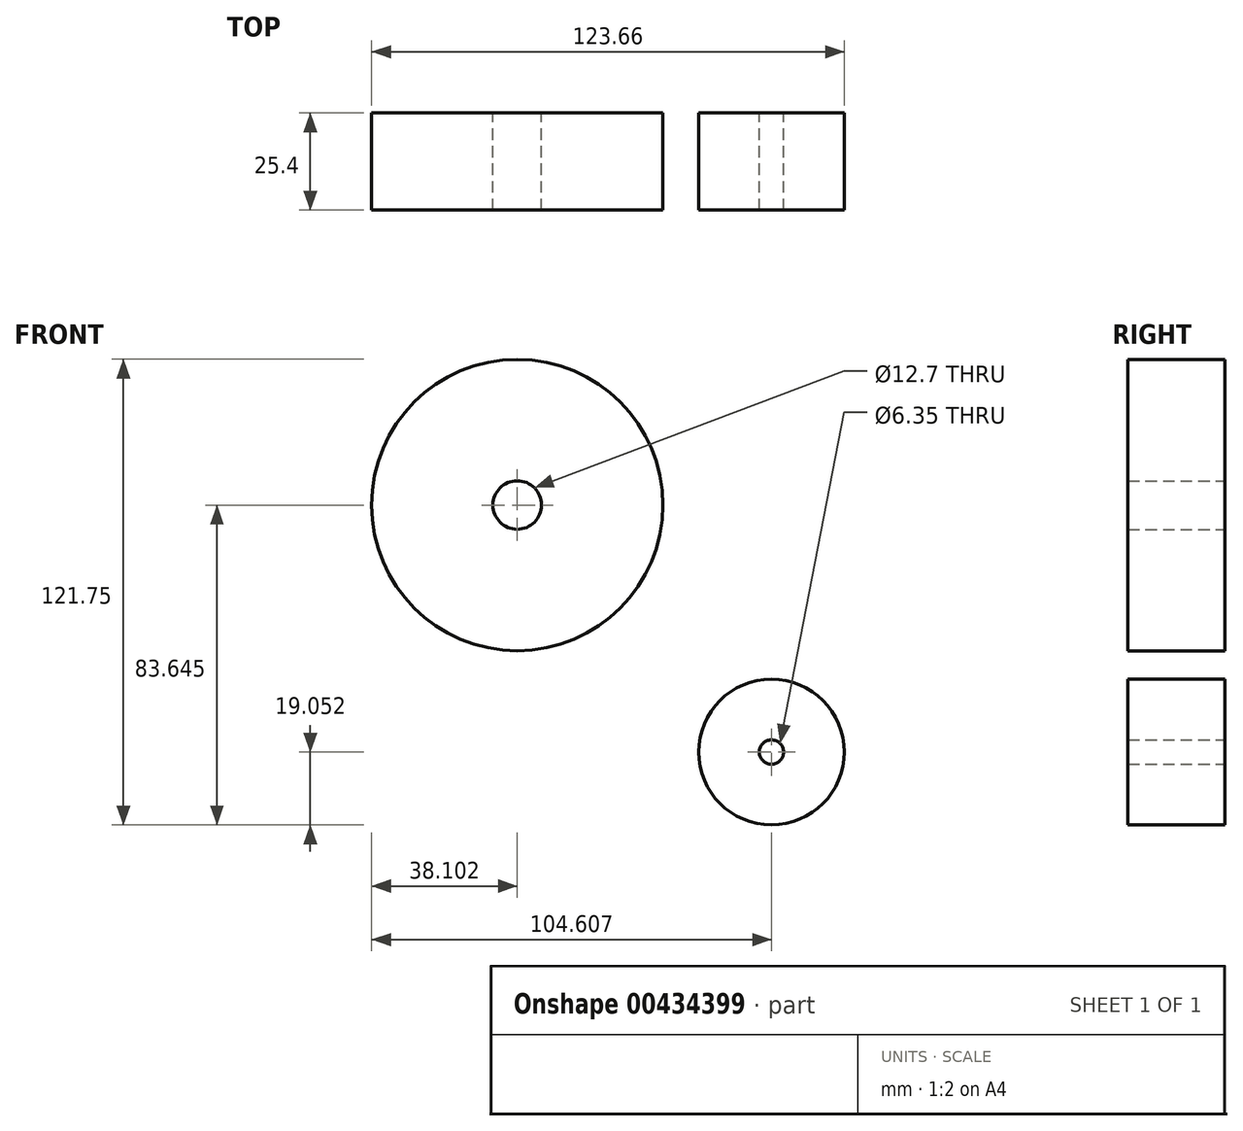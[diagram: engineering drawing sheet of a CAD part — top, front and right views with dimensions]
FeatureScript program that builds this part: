
annotation { "Feature Type Name" : "Feature", "Feature Type Description" : "" }
export const myFeature = defineFeature(function(context is Context, id is Id, definition is map)
    precondition{}
    {
        {
            var Q0;
            Q0=qCreatedBy(makeId("Front.planeOp"),FACE);
            var sketch = newSketch(context, id + "F0", { "sketchPlane" : qUnion([Q0])});
            skCircle(sketch, "E0", {"center": v(-37.84, 38.9) * mm, "radius": 38.1 * mm});
            skCircle(sketch, "E1", {"center": v(28.67, -25.7) * mm, "radius": 19.05 * mm});
            skCircle(sketch, "E2", {"center": v(-37.84, 38.9) * mm, "radius": 6.35 * mm});
            skCircle(sketch, "E3", {"center": v(28.67, -25.7) * mm, "radius": 3.18 * mm});
            skLineSegment(sketch, "E4", {"start": v(9.27, 45.7) * mm, "end": v(10.58, 44.4) * mm});
            skLineSegment(sketch, "E5", {"start": v(10.58, 44.4) * mm, "end": v(7.68, 40.25) * mm});
            skLineSegment(sketch, "E6", {"start": v(7.68, 40.25) * mm, "end": v(5.12, 42.8) * mm});
            skLineSegment(sketch, "E7", {"start": v(5.12, 42.8) * mm, "end": v(9.27, 45.7) * mm});
            skSolve(sketch);
        }
        {
            var Q0;
            Q0=makeQuery(id+"F0.imprint","IMPRINT",FACE,{"disambiguationData":[TD([[makeQuery(id+"F0.imprint","IMPRINT",EDGE,{"derivedFrom":sQuery(id+"F0.wireOp",EDGE,"E0")}),1.0]])]});
            var Q1;
            Q1=makeQuery(id+"F0.imprint","IMPRINT",FACE,{"disambiguationData":[TD([[makeQuery(id+"F0.imprint","IMPRINT",EDGE,{"derivedFrom":sQuery(id+"F0.wireOp",EDGE,"E1")}),1.0]])]});
            extrude(context, id + "F1", {"entities" : qUnion([Q0, Q1]), "depth" : 25.4 * mm});
        }
    });
